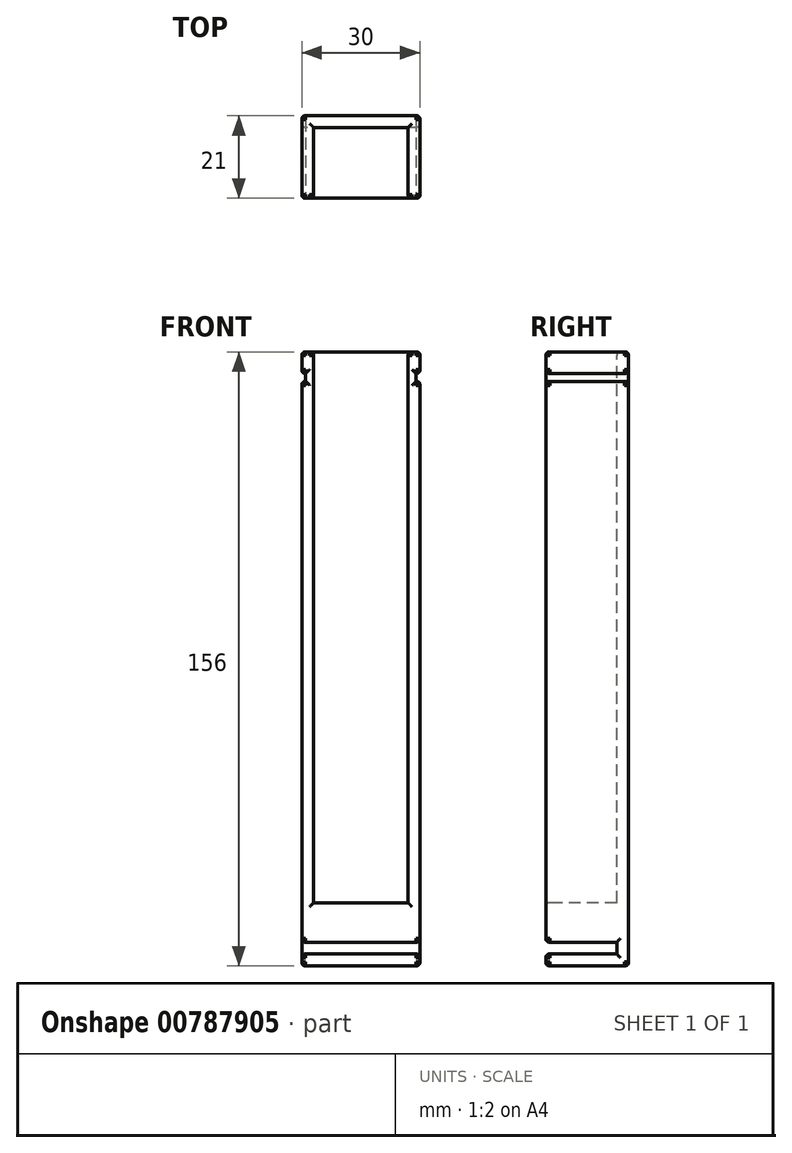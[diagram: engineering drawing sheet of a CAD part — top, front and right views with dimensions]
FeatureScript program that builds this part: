
annotation { "Feature Type Name" : "Feature", "Feature Type Description" : "" }
export const myFeature = defineFeature(function(context is Context, id is Id, definition is map)
    precondition{}
    {
        {
            var Q0;
            Q0=qCreatedBy(makeId("Top.planeOp"),FACE);
            var sketch = newSketch(context, id + "F0", { "sketchPlane" : qUnion([Q0])});
            skLineSegment(sketch, "E0.bottom", {"start": v(-15, 10.5) * mm, "end": v(15, 10.5) * mm});
            skLineSegment(sketch, "E0.top", {"start": v(-15, -10.5) * mm, "end": v(15, -10.5) * mm});
            skLineSegment(sketch, "E0.left", {"start": v(-15, 10.5) * mm, "end": v(-15, -10.5) * mm});
            skLineSegment(sketch, "E0.right", {"start": v(15, 10.5) * mm, "end": v(15, -10.5) * mm});
            skPoint(sketch, "E0.middle", {"position": v(0, 0) * mm});
            skSolve(sketch);
        }
        {
            var Q0;
            Q0 = qSketchRegion(id + "F0", true);
            extrude(context, id + "F1", {"entities" : qUnion([Q0]), "depth" : 156 * mm, "offsetDistance" : 25.4 * mm});
        }
        {
            var Q0;
            Q0=makeQuery(id+"F1.opExtrude","SWEPT_FACE",FACE,{"disambiguationData":[OSD([sQuery(id+"F0.wireOp",EDGE,"E0.top")])]});
            var sketch = newSketch(context, id + "F2", { "sketchPlane" : qUnion([Q0])});
            skLineSegment(sketch, "E1.bottom", {"start": v(15, 6) * mm, "end": v(-15, 6) * mm});
            skLineSegment(sketch, "E1.top", {"start": v(15, 3) * mm, "end": v(-15, 3) * mm});
            skLineSegment(sketch, "E1.left", {"start": v(15, 6) * mm, "end": v(15, 3) * mm});
            skLineSegment(sketch, "E1.right", {"start": v(-15, 6) * mm, "end": v(-15, 3) * mm});
            skPoint(sketch, "E1.middle", {"position": v(0, 4.5) * mm});
            skSolve(sketch);
        }
        {
            var Q0;
            Q0 = qSketchRegion(id + "F2", true);
            extrude(context, id + "F3", {"entities" : qUnion([Q0]), "operationType" : NewBodyOperationType.REMOVE, "oppositeDirection" : true, "depth" : 18 * mm, "offsetDistance" : 25.4 * mm, "hasDraft" : true, "draftAngle" : 0 * degree});
        }
        {
            var Q0;
            Q0=makeQuery(id+"F1.opExtrude","CAP_FACE",FACE,{"disambiguationData":[OSD([sQuery(id+"F0.wireOp",EDGE,"E0.bottom"),sQuery(id+"F0.wireOp",EDGE,"E0.top"),sQuery(id+"F0.wireOp",EDGE,"E0.left"),sQuery(id+"F0.wireOp",EDGE,"E0.right")])],"isStart":false});
            var sketch = newSketch(context, id + "F4", { "sketchPlane" : qUnion([Q0])});
            skLineSegment(sketch, "E2.bottom", {"start": v(-12, 7.5) * mm, "end": v(12, 7.5) * mm});
            skLineSegment(sketch, "E2.top", {"start": v(-12, -10.5) * mm, "end": v(12, -10.5) * mm});
            skLineSegment(sketch, "E2.left", {"start": v(-12, 7.5) * mm, "end": v(-12, -10.5) * mm});
            skLineSegment(sketch, "E2.right", {"start": v(12, 7.5) * mm, "end": v(12, -10.5) * mm});
            skLineSegment(sketch, "E3.bottom", {"start": v(15, 10.5) * mm, "end": v(-15, 10.5) * mm});
            skLineSegment(sketch, "E3.top", {"start": v(15, -10.5) * mm, "end": v(-15, -10.5) * mm});
            skLineSegment(sketch, "E3.left", {"start": v(15, 10.5) * mm, "end": v(15, -10.5) * mm});
            skLineSegment(sketch, "E3.right", {"start": v(-15, 10.5) * mm, "end": v(-15, -10.5) * mm});
            skPoint(sketch, "E3.middle", {"position": v(0, 0) * mm});
            skSolve(sketch);
        }
        {
            var Q0;
            Q0=makeQuery(id+"F4.imprint","IMPRINT",FACE,{"disambiguationData":[TD([[makeQuery(id+"F4.imprint","IMPRINT",EDGE,{"derivedFrom":sQuery(id+"F4.wireOp",EDGE,"E2.bottom")}),-1.0]])]});
            extrude(context, id + "F5", {"entities" : qUnion([Q0]), "operationType" : NewBodyOperationType.REMOVE, "oppositeDirection" : true, "depth" : 140 * mm, "offsetDistance" : 25.4 * mm});
        }
        {
            var Q0;
            Q0=makeQuery(id+"F1.opExtrude","SWEPT_FACE",FACE,{"disambiguationData":[OSD([sQuery(id+"F0.wireOp",EDGE,"E0.right")])]});
            var sketch = newSketch(context, id + "F6", { "sketchPlane" : qUnion([Q0])});
            skLineSegment(sketch, "E4.bottom", {"start": v(-10.5, 150.5) * mm, "end": v(10.5, 150.5) * mm});
            skLineSegment(sketch, "E4.top", {"start": v(-10.5, 148.5) * mm, "end": v(10.5, 148.5) * mm});
            skLineSegment(sketch, "E4.left", {"start": v(-10.5, 150.5) * mm, "end": v(-10.5, 148.5) * mm});
            skLineSegment(sketch, "E4.right", {"start": v(10.5, 150.5) * mm, "end": v(10.5, 148.5) * mm});
            skLineSegment(sketch, "E5", {"start": v(-10.5, 156) * mm, "end": v(10.5, 156) * mm});
            skSolve(sketch);
        }
        {
            var Q0;
            Q0=makeQuery(id+"F6.imprint","IMPRINT",FACE,{"disambiguationData":[TD([[makeQuery(id+"F6.imprint","IMPRINT",EDGE,{"derivedFrom":sQuery(id+"F6.wireOp",EDGE,"E4.bottom")}),-1.0]])]});
            extrude(context, id + "F7", {"entities" : qUnion([Q0]), "operationType" : NewBodyOperationType.REMOVE, "oppositeDirection" : true, "depth" : 1 * mm, "offsetDistance" : 25.4 * mm});
        }
        {
            var Q0;
            Q0=makeQuery(id+"F1.opExtrude","SWEPT_FACE",FACE,{"disambiguationData":[OSD([sQuery(id+"F0.wireOp",EDGE,"E0.left")])]});
            var sketch = newSketch(context, id + "F8", { "sketchPlane" : qUnion([Q0])});
            skLineSegment(sketch, "E6.bottom", {"start": v(-10.5, 148.5) * mm, "end": v(10.5, 148.5) * mm});
            skLineSegment(sketch, "E6.top", {"start": v(-10.5, 150.5) * mm, "end": v(10.5, 150.5) * mm});
            skLineSegment(sketch, "E6.left", {"start": v(-10.5, 148.5) * mm, "end": v(-10.5, 150.5) * mm});
            skLineSegment(sketch, "E6.right", {"start": v(10.5, 148.5) * mm, "end": v(10.5, 150.5) * mm});
            skLineSegment(sketch, "E7", {"start": v(10.5, 156) * mm, "end": v(-10.5, 156) * mm});
            skSolve(sketch);
        }
        {
            var Q0;
            Q0=makeQuery(id+"F8.imprint","IMPRINT",FACE,{"disambiguationData":[TD([[makeQuery(id+"F8.imprint","IMPRINT",EDGE,{"derivedFrom":sQuery(id+"F8.wireOp",EDGE,"E6.bottom")}),1.0]])]});
            extrude(context, id + "F9", {"entities" : qUnion([Q0]), "operationType" : NewBodyOperationType.REMOVE, "oppositeDirection" : true, "depth" : 1 * mm, "offsetDistance" : 25.4 * mm});
        }
        {
            var Q0;
            {var subQ2=sQuery(id+"F0.wireOp",EDGE,"E0.top");Q0=makeQuery(id+"F3.boolean.opBoolean","SPLIT",FACE,{"disambiguationData":[TD([makeQuery(id+"F3.opExtrude","SWEPT_FACE",FACE,{"disambiguationData":[OSD([sQuery(id+"F2.wireOp",EDGE,"E1.top")])]})])],"derivedFrom":makeQuery(id+"F1.opExtrude","SWEPT_FACE",FACE,{"disambiguationData":[OSD([subQ2])]})});}
            var Q1;
            {var subQ2=sQuery(id+"F0.wireOp",EDGE,"E0.top");Q1=makeQuery(id+"F3.boolean.opBoolean","SPLIT",FACE,{"disambiguationData":[TD([makeQuery(id+"F3.opExtrude","SWEPT_FACE",FACE,{"disambiguationData":[OSD([sQuery(id+"F2.wireOp",EDGE,"E1.bottom")])]})])],"derivedFrom":makeQuery(id+"F1.opExtrude","SWEPT_FACE",FACE,{"disambiguationData":[OSD([subQ2])]})});}
            var Q2;
            {var subQ1=sQuery(id+"F2.wireOp",EDGE,"E1.bottom");var subQ3=sQuery(id+"F0.wireOp",EDGE,"E0.right");Q2=makeQuery(id+"F7.boolean.opBoolean","SPLIT",FACE,{"disambiguationData":[TD([makeQuery(id+"F3.boolean.opBoolean","COPY",FACE,{"derivedFrom":makeQuery(id+"F3.opExtrude","SWEPT_FACE",FACE,{"disambiguationData":[OSD([subQ1])]})})])],"derivedFrom":makeQuery(id+"F1.opExtrude","SWEPT_FACE",FACE,{"disambiguationData":[OSD([subQ3])]})});}
            var Q3;
            {var subQ1=sQuery(id+"F2.wireOp",EDGE,"E1.bottom");var subQ3=sQuery(id+"F0.wireOp",EDGE,"E0.left");Q3=makeQuery(id+"F9.boolean.opBoolean","SPLIT",FACE,{"disambiguationData":[TD([makeQuery(id+"F3.boolean.opBoolean","COPY",FACE,{"derivedFrom":makeQuery(id+"F3.opExtrude","SWEPT_FACE",FACE,{"disambiguationData":[OSD([subQ1])]})})])],"derivedFrom":makeQuery(id+"F1.opExtrude","SWEPT_FACE",FACE,{"disambiguationData":[OSD([subQ3])]})});}
            var Q4;
            Q4=makeQuery(id+"F1.opExtrude","SWEPT_FACE",FACE,{"disambiguationData":[OSD([sQuery(id+"F0.wireOp",EDGE,"E0.bottom")])]});
            var Q5;
            {var subQ1=sQuery(id+"F0.wireOp",EDGE,"E0.left");Q5=makeQuery(id+"F9.boolean.opBoolean","SPLIT",FACE,{"disambiguationData":[TD([makeQuery(id+"F9.opExtrude","SWEPT_FACE",FACE,{"disambiguationData":[OSD([sQuery(id+"F8.wireOp",EDGE,"E6.top")])]})])],"derivedFrom":makeQuery(id+"F1.opExtrude","SWEPT_FACE",FACE,{"disambiguationData":[OSD([subQ1])]})});}
            var Q6;
            Q6=makeQuery(id+"F1.opExtrude","CAP_FACE",FACE,{"disambiguationData":[OSD([sQuery(id+"F0.wireOp",EDGE,"E0.bottom"),sQuery(id+"F0.wireOp",EDGE,"E0.top"),sQuery(id+"F0.wireOp",EDGE,"E0.left"),sQuery(id+"F0.wireOp",EDGE,"E0.right")])],"isStart":false});
            var Q7;
            {var subQ1=sQuery(id+"F0.wireOp",EDGE,"E0.right");Q7=makeQuery(id+"F7.boolean.opBoolean","SPLIT",FACE,{"disambiguationData":[TD([makeQuery(id+"F7.opExtrude","SWEPT_FACE",FACE,{"disambiguationData":[OSD([sQuery(id+"F6.wireOp",EDGE,"E4.bottom")])]})])],"derivedFrom":makeQuery(id+"F1.opExtrude","SWEPT_FACE",FACE,{"disambiguationData":[OSD([subQ1])]})});}
            var Q8;
            Q8=makeQuery(id+"F1.opExtrude","CAP_FACE",FACE,{"disambiguationData":[OSD([sQuery(id+"F0.wireOp",EDGE,"E0.bottom"),sQuery(id+"F0.wireOp",EDGE,"E0.top"),sQuery(id+"F0.wireOp",EDGE,"E0.left"),sQuery(id+"F0.wireOp",EDGE,"E0.right")])],"isStart":true});
            fillet(context, id + "F10", {"entities" : qUnion([Q0, Q1, Q2, Q3, Q4, Q5, Q6, Q7, Q8]), "radius" : 1 * mm, "tangentPropagation" : true, "rho" : 0.5, "crossSection" : FilletCrossSection.CONIC, "allowEdgeOverflow" : false});
        }
    });
